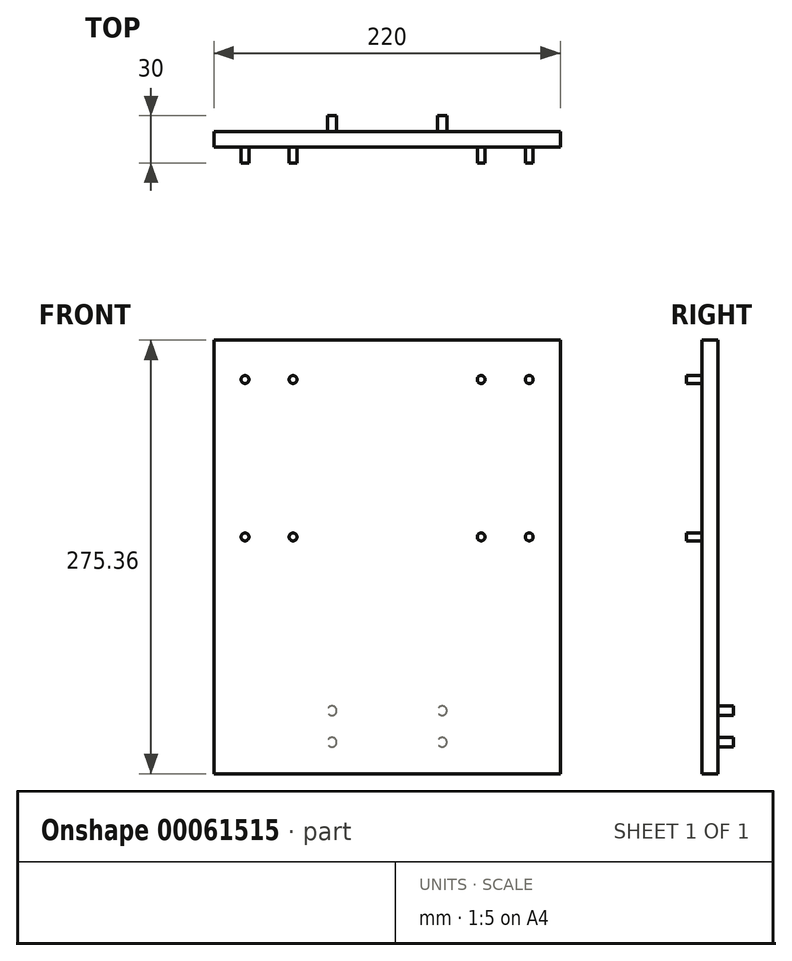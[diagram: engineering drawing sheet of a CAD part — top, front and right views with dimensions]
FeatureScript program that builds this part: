
annotation { "Feature Type Name" : "Feature", "Feature Type Description" : "" }
export const myFeature = defineFeature(function(context is Context, id is Id, definition is map)
    precondition{}
    {
        {
            var Q0;
            Q0=qCreatedBy(makeId("Front.planeOp"),FACE);
            var sketch = newSketch(context, id + "F0", { "sketchPlane" : qUnion([Q0])});
            skLineSegment(sketch, "E0.bottom", {"start": v(-110, 132.27) * mm, "end": v(110, 132.27) * mm});
            skLineSegment(sketch, "E0.top", {"start": v(-110, -143.09) * mm, "end": v(110, -143.09) * mm});
            skLineSegment(sketch, "E0.left", {"start": v(-110, 132.27) * mm, "end": v(-110, -143.09) * mm});
            skLineSegment(sketch, "E0.right", {"start": v(110, 132.27) * mm, "end": v(110, -143.09) * mm});
            skCircle(sketch, "E1", {"center": v(-90.25, 107.27) * mm, "radius": 2.5 * mm});
            skCircle(sketch, "E2", {"center": v(-59.75, 107.27) * mm, "radius": 2.5 * mm});
            skLineSegment(sketch, "E3", {"start": v(-90.25, 107.27) * mm, "end": v(-59.75, 107.27) * mm, "construction": true});
            skCircle(sketch, "E4", {"center": v(-90.25, 7.27) * mm, "radius": 2.5 * mm});
            skCircle(sketch, "E5", {"center": v(-59.75, 7.27) * mm, "radius": 2.5 * mm});
            skLineSegment(sketch, "E6", {"start": v(-90.25, 7.27) * mm, "end": v(-59.75, 7.27) * mm, "construction": true});
            skCircle(sketch, "E7", {"center": v(59.75, 107.27) * mm, "radius": 2.5 * mm});
            skCircle(sketch, "E8", {"center": v(90.25, 107.27) * mm, "radius": 2.5 * mm});
            skLineSegment(sketch, "E9", {"start": v(59.75, 107.27) * mm, "end": v(90.25, 107.27) * mm, "construction": true});
            skCircle(sketch, "E10", {"center": v(59.75, 7.27) * mm, "radius": 2.5 * mm});
            skCircle(sketch, "E11", {"center": v(90.25, 7.27) * mm, "radius": 2.5 * mm});
            skLineSegment(sketch, "E12", {"start": v(59.75, 7.27) * mm, "end": v(90.25, 7.27) * mm, "construction": true});
            skLineSegment(sketch, "E13", {"start": v(-75, 107.27) * mm, "end": v(-75, 7.27) * mm, "construction": true});
            skLineSegment(sketch, "E14", {"start": v(75, 107.27) * mm, "end": v(75, 7.27) * mm, "construction": true});
            skLineSegment(sketch, "E15", {"start": v(0, 132.27) * mm, "end": v(0, -143.09) * mm, "construction": true});
            skSolve(sketch);
        }
        {
            var Q0;
            Q0=makeQuery(id+"F0.imprint","IMPRINT",FACE,{"disambiguationData":[TD([[makeQuery(id+"F0.imprint","IMPRINT",EDGE,{"derivedFrom":sQuery(id+"F0.wireOp",EDGE,"E0.bottom")}),-1.0]])]});
            var Q1;
            Q1=makeQuery(id+"F0.imprint","IMPRINT",FACE,{"disambiguationData":[TD([[makeQuery(id+"F0.imprint","IMPRINT",EDGE,{"derivedFrom":sQuery(id+"F0.wireOp",EDGE,"E1")}),1.0]])]});
            var Q2;
            Q2=makeQuery(id+"F0.imprint","IMPRINT",FACE,{"disambiguationData":[TD([[makeQuery(id+"F0.imprint","IMPRINT",EDGE,{"derivedFrom":sQuery(id+"F0.wireOp",EDGE,"E2")}),1.0]])]});
            var Q3;
            Q3=makeQuery(id+"F0.imprint","IMPRINT",FACE,{"disambiguationData":[TD([[makeQuery(id+"F0.imprint","IMPRINT",EDGE,{"derivedFrom":sQuery(id+"F0.wireOp",EDGE,"E4")}),1.0]])]});
            var Q4;
            Q4=makeQuery(id+"F0.imprint","IMPRINT",FACE,{"disambiguationData":[TD([[makeQuery(id+"F0.imprint","IMPRINT",EDGE,{"derivedFrom":sQuery(id+"F0.wireOp",EDGE,"E5")}),1.0]])]});
            var Q5;
            Q5=makeQuery(id+"F0.imprint","IMPRINT",FACE,{"disambiguationData":[TD([[makeQuery(id+"F0.imprint","IMPRINT",EDGE,{"derivedFrom":sQuery(id+"F0.wireOp",EDGE,"E10")}),1.0]])]});
            var Q6;
            Q6=makeQuery(id+"F0.imprint","IMPRINT",FACE,{"disambiguationData":[TD([[makeQuery(id+"F0.imprint","IMPRINT",EDGE,{"derivedFrom":sQuery(id+"F0.wireOp",EDGE,"E11")}),1.0]])]});
            var Q7;
            Q7=makeQuery(id+"F0.imprint","IMPRINT",FACE,{"disambiguationData":[TD([[makeQuery(id+"F0.imprint","IMPRINT",EDGE,{"derivedFrom":sQuery(id+"F0.wireOp",EDGE,"E7")}),1.0]])]});
            var Q8;
            Q8=makeQuery(id+"F0.imprint","IMPRINT",FACE,{"disambiguationData":[TD([[makeQuery(id+"F0.imprint","IMPRINT",EDGE,{"derivedFrom":sQuery(id+"F0.wireOp",EDGE,"E8")}),1.0]])]});
            extrude(context, id + "F1", {"entities" : qUnion([Q0, Q1, Q2, Q3, Q4, Q5, Q6, Q7, Q8]), "oppositeDirection" : true, "depth" : 10 * mm});
        }
        {
            var Q0;
            Q0=makeQuery(id+"F0.imprint","IMPRINT",FACE,{"disambiguationData":[TD([[makeQuery(id+"F0.imprint","IMPRINT",EDGE,{"derivedFrom":sQuery(id+"F0.wireOp",EDGE,"E8")}),1.0]])]});
            var Q1;
            Q1=makeQuery(id+"F0.imprint","IMPRINT",FACE,{"disambiguationData":[TD([[makeQuery(id+"F0.imprint","IMPRINT",EDGE,{"derivedFrom":sQuery(id+"F0.wireOp",EDGE,"E7")}),1.0]])]});
            var Q2;
            Q2=makeQuery(id+"F0.imprint","IMPRINT",FACE,{"disambiguationData":[TD([[makeQuery(id+"F0.imprint","IMPRINT",EDGE,{"derivedFrom":sQuery(id+"F0.wireOp",EDGE,"E2")}),1.0]])]});
            var Q3;
            Q3=makeQuery(id+"F0.imprint","IMPRINT",FACE,{"disambiguationData":[TD([[makeQuery(id+"F0.imprint","IMPRINT",EDGE,{"derivedFrom":sQuery(id+"F0.wireOp",EDGE,"E1")}),1.0]])]});
            var Q4;
            Q4=makeQuery(id+"F0.imprint","IMPRINT",FACE,{"disambiguationData":[TD([[makeQuery(id+"F0.imprint","IMPRINT",EDGE,{"derivedFrom":sQuery(id+"F0.wireOp",EDGE,"E11")}),1.0]])]});
            var Q5;
            Q5=makeQuery(id+"F0.imprint","IMPRINT",FACE,{"disambiguationData":[TD([[makeQuery(id+"F0.imprint","IMPRINT",EDGE,{"derivedFrom":sQuery(id+"F0.wireOp",EDGE,"E10")}),1.0]])]});
            var Q6;
            Q6=makeQuery(id+"F0.imprint","IMPRINT",FACE,{"disambiguationData":[TD([[makeQuery(id+"F0.imprint","IMPRINT",EDGE,{"derivedFrom":sQuery(id+"F0.wireOp",EDGE,"E4")}),1.0]])]});
            var Q7;
            Q7=makeQuery(id+"F0.imprint","IMPRINT",FACE,{"disambiguationData":[TD([[makeQuery(id+"F0.imprint","IMPRINT",EDGE,{"derivedFrom":sQuery(id+"F0.wireOp",EDGE,"E5")}),1.0]])]});
            extrude(context, id + "F2", {"entities" : qUnion([Q0, Q1, Q2, Q3, Q4, Q5, Q6, Q7]), "operationType" : NewBodyOperationType.ADD, "depth" : 10 * mm});
        }
        {
            var Q0;
            Q0=makeQuery(id+"F0.imprint","IMPRINT",FACE,{"disambiguationData":[TD([[makeQuery(id+"F0.imprint","IMPRINT",EDGE,{"derivedFrom":sQuery(id+"F0.wireOp",EDGE,"E0.bottom")}),-1.0]])]});
            var sketch = newSketch(context, id + "F3", { "sketchPlane" : qUnion([Q0])});
            skCircle(sketch, "E16", {"center": v(35, -123.09) * mm, "radius": 3 * mm});
            skLineSegment(sketch, "E17.bottom", {"start": v(35, -123.09) * mm, "end": v(-35, -123.09) * mm, "construction": true});
            skLineSegment(sketch, "E17.top", {"start": v(35, -103.09) * mm, "end": v(-35, -103.09) * mm, "construction": true});
            skLineSegment(sketch, "E17.left", {"start": v(35, -123.09) * mm, "end": v(35, -103.09) * mm, "construction": true});
            skLineSegment(sketch, "E17.right", {"start": v(-35, -123.09) * mm, "end": v(-35, -103.09) * mm, "construction": true});
            skCircle(sketch, "E18", {"center": v(35, -103.09) * mm, "radius": 3 * mm});
            skCircle(sketch, "E19", {"center": v(-35, -103.09) * mm, "radius": 3 * mm});
            skCircle(sketch, "E20", {"center": v(-35, -123.09) * mm, "radius": 3 * mm});
            skSolve(sketch);
        }
        {
            var Q0;
            Q0=makeQuery(id+"F3.imprint","IMPRINT",FACE,{"disambiguationData":[TD([[makeQuery(id+"F3.imprint","IMPRINT",EDGE,{"derivedFrom":sQuery(id+"F3.wireOp",EDGE,"E18")}),1.0]])]});
            var Q1;
            Q1=makeQuery(id+"F3.imprint","IMPRINT",FACE,{"disambiguationData":[TD([[makeQuery(id+"F3.imprint","IMPRINT",EDGE,{"derivedFrom":sQuery(id+"F3.wireOp",EDGE,"E16")}),1.0]])]});
            var Q2;
            Q2=makeQuery(id+"F3.imprint","IMPRINT",FACE,{"disambiguationData":[TD([[makeQuery(id+"F3.imprint","IMPRINT",EDGE,{"derivedFrom":sQuery(id+"F3.wireOp",EDGE,"E20")}),1.0]])]});
            var Q3;
            Q3=makeQuery(id+"F3.imprint","IMPRINT",FACE,{"disambiguationData":[TD([[makeQuery(id+"F3.imprint","IMPRINT",EDGE,{"derivedFrom":sQuery(id+"F3.wireOp",EDGE,"E19")}),1.0]])]});
            extrude(context, id + "F4", {"entities" : qUnion([Q0, Q1, Q2, Q3]), "operationType" : NewBodyOperationType.ADD, "oppositeDirection" : true, "depth" : 20 * mm});
        }
    });
